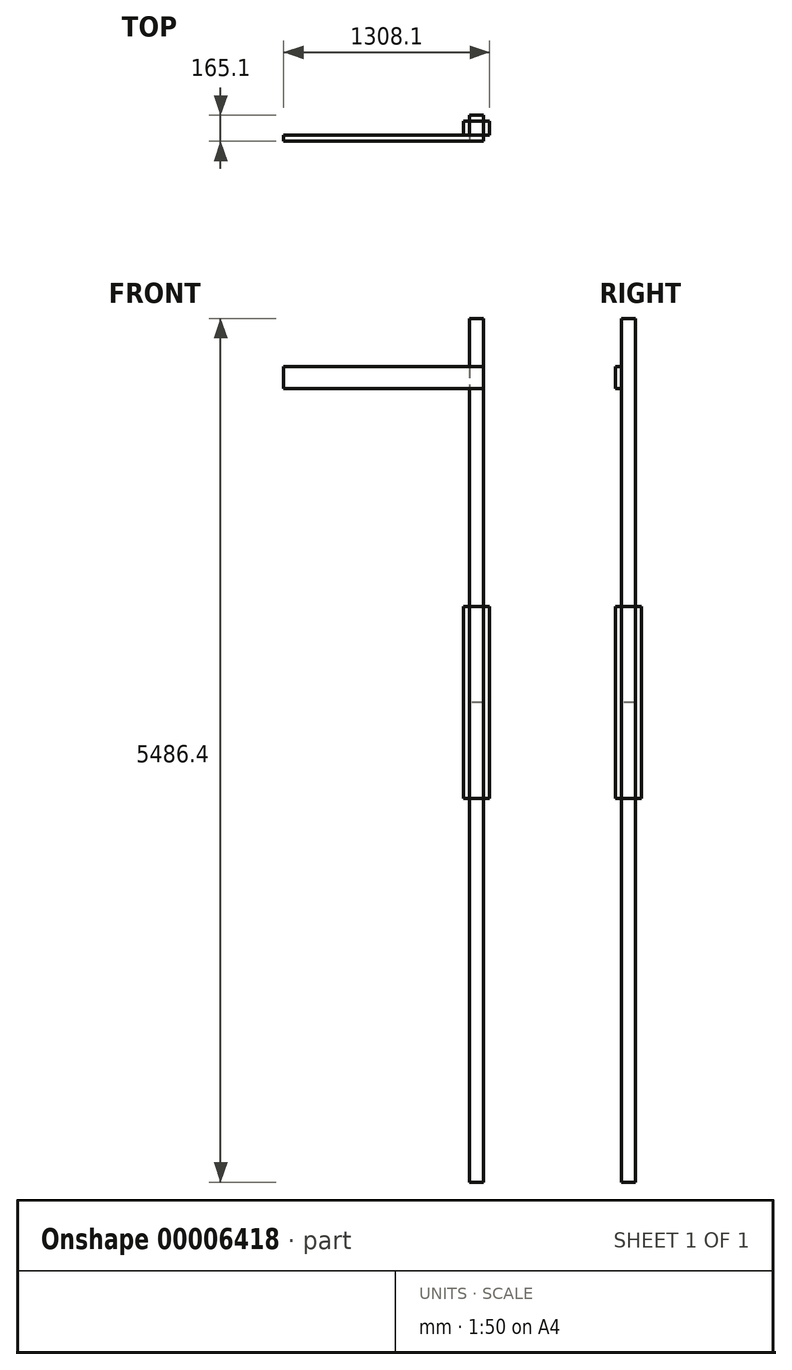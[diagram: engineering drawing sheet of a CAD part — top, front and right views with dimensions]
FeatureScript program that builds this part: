
annotation { "Feature Type Name" : "Feature", "Feature Type Description" : "" }
export const myFeature = defineFeature(function(context is Context, id is Id, definition is map)
    precondition{}
    {
        {
            var Q0;
            Q0=qCreatedBy(makeId("Top.planeOp"),FACE);
            var sketch = newSketch(context, id + "F0", { "sketchPlane" : qUnion([Q0])});
            skLineSegment(sketch, "E0.rect.bottom", {"start": v(44.45, 44.45) * mm, "end": v(-44.45, 44.45) * mm});
            skLineSegment(sketch, "E0.rect.top", {"start": v(44.45, -44.45) * mm, "end": v(-44.45, -44.45) * mm});
            skLineSegment(sketch, "E0.rect.left", {"start": v(44.45, 44.45) * mm, "end": v(44.45, -44.45) * mm});
            skLineSegment(sketch, "E0.rect.right", {"start": v(-44.45, 44.45) * mm, "end": v(-44.45, -44.45) * mm});
            skPoint(sketch, "E0.rect.middle", {"position": v(0, 0) * mm});
            skSolve(sketch);
        }
        {
            var Q0;
            Q0=makeQuery(id+"F0.imprint","IMPRINT",FACE,{"disambiguationData":[TD([[makeQuery(id+"F0.imprint","IMPRINT",EDGE,{"derivedFrom":sQuery(id+"F0.wireOp",EDGE,"E0.rect.bottom")}),1.0]])]});
            extrude(context, id + "F1", {"entities" : qUnion([Q0]), "depth" : 3048 * mm});
        }
        {
            var Q0;
            Q0=makeQuery(id+"F1.opExtrude","CAP_FACE",FACE,{"disambiguationData":[OSD([sQuery(id+"F0.wireOp",EDGE,"E0.rect.bottom"),sQuery(id+"F0.wireOp",EDGE,"E0.rect.top"),sQuery(id+"F0.wireOp",EDGE,"E0.rect.left"),sQuery(id+"F0.wireOp",EDGE,"E0.rect.right")])],"isStart":false});
            cPlane(context, id + "F2", {"entities" : qUnion([Q0]), "cplaneType" : CPlaneType.OFFSET, "offset" : 609.6 * mm, "oppositeDirection" : true, "width" : 152.4 * mm, "height" : 152.4 * mm});
        }
        {
            var Q0;
            Q0=qCreatedBy(id+"F2.planeOp",FACE);
            var sketch = newSketch(context, id + "F3", { "sketchPlane" : qUnion([Q0])});
            skLineSegment(sketch, "E1.0.0", {"start": v(44.45, 44.45) * mm, "end": v(44.45, -44.45) * mm});
            skLineSegment(sketch, "E2.bottom", {"start": v(44.45, -44.45) * mm, "end": v(82.55, -44.45) * mm});
            skLineSegment(sketch, "E2.top", {"start": v(44.45, 44.45) * mm, "end": v(82.55, 44.45) * mm});
            skLineSegment(sketch, "E2.left", {"start": v(44.45, -44.45) * mm, "end": v(44.45, 44.45) * mm});
            skLineSegment(sketch, "E2.right", {"start": v(82.55, -44.45) * mm, "end": v(82.55, 44.45) * mm});
            skSolve(sketch);
        }
        {
            var Q0;
            Q0=makeQuery(id+"F3.imprint","IMPRINT",FACE,{"disambiguationData":[TD([[makeQuery(id+"F3.imprint","IMPRINT",EDGE,{"derivedFrom":sQuery(id+"F3.wireOp",EDGE,"E2.bottom")}),1.0]])]});
            extrude(context, id + "F4", {"entities" : qUnion([Q0]), "depth" : 1219.2 * mm});
        }
        {
            var Q0;
            Q0=qCreatedBy(makeId("Front.planeOp"),FACE);
            var sketch = newSketch(context, id + "F5", { "sketchPlane" : qUnion([Q0])});
            skLineSegment(sketch, "E3", {"start": v(0, 0) * mm, "end": v(0, -138.6) * mm, "construction": true});
            skSolve(sketch);
        }
        {
            var Q0;
            Q0=makeQuery(id+"F1.opExtrude","CAP_FACE",FACE,{"disambiguationData":[OSD([sQuery(id+"F0.wireOp",EDGE,"E0.rect.bottom"),sQuery(id+"F0.wireOp",EDGE,"E0.rect.top"),sQuery(id+"F0.wireOp",EDGE,"E0.rect.left"),sQuery(id+"F0.wireOp",EDGE,"E0.rect.right")])],"isStart":false});
            var sketch = newSketch(context, id + "F6", { "sketchPlane" : qUnion([Q0])});
            skLineSegment(sketch, "E4.bottom", {"start": v(-44.45, -44.45) * mm, "end": v(44.45, -44.45) * mm});
            skLineSegment(sketch, "E4.top", {"start": v(-44.45, 44.45) * mm, "end": v(44.45, 44.45) * mm});
            skLineSegment(sketch, "E4.left", {"start": v(-44.45, -44.45) * mm, "end": v(-44.45, 44.45) * mm});
            skLineSegment(sketch, "E4.right", {"start": v(44.45, -44.45) * mm, "end": v(44.45, 44.45) * mm});
            skSolve(sketch);
        }
        {
            var Q0;
            Q0=makeQuery(id+"F6.imprint","IMPRINT",FACE,{"disambiguationData":[TD([[makeQuery(id+"F6.imprint","IMPRINT",EDGE,{"derivedFrom":sQuery(id+"F6.wireOp",EDGE,"E4.bottom")}),-1.0]])]});
            extrude(context, id + "F7", {"entities" : qUnion([Q0]), "depth" : 2438.4 * mm});
        }
        {
            var Q0;
            Q0=makeQuery(id+"F4.opExtrude","SWEPT_BODY",BODY,{"disambiguationData":[OSD([sQuery(id+"F3.wireOp",EDGE,"E2.bottom"),sQuery(id+"F3.wireOp",EDGE,"E2.top"),sQuery(id+"F3.wireOp",EDGE,"E2.left"),sQuery(id+"F3.wireOp",EDGE,"E2.right")])]});
            var Q1;
            Q1=makeQuery(id+"FR1GvV9cY72cUo5_3.opExtrude","SWEPT_BODY",BODY,{"disambiguationData":[OSD([sQuery(id+"Fx0JtN3gMRifMKx_3.wireOp",EDGE,"1e4fa40f-9285-4ff4-9127-986e21447ed7.bottom"),sQuery(id+"Fx0JtN3gMRifMKx_3.wireOp",EDGE,"1e4fa40f-9285-4ff4-9127-986e21447ed7.top"),sQuery(id+"Fx0JtN3gMRifMKx_3.wireOp",EDGE,"1e4fa40f-9285-4ff4-9127-986e21447ed7.left"),sQuery(id+"Fx0JtN3gMRifMKx_3.wireOp",EDGE,"1e4fa40f-9285-4ff4-9127-986e21447ed7.right")])]});
            var Q2;
            Q2=sQuery(id+"F5.wireOp",EDGE,"E3");
            circularPattern(context, id + "F8", {"entities" : qUnion([Q0, Q1]), "axis" : qUnion([Q2]), "angle" : 90 * degree, "instanceCount" : round(4)});
        }
        {
            var Q0;
            Q0=makeQuery(id+"F7.opExtrude","SWEPT_FACE",FACE,{"disambiguationData":[OSD([sQuery(id+"F6.wireOp",EDGE,"E4.bottom")])]});
            var sketch = newSketch(context, id + "F9", { "sketchPlane" : qUnion([Q0])});
            skLineSegment(sketch, "E5.bottom", {"start": v(44.45, 5181.6) * mm, "end": v(-1225.55, 5181.6) * mm});
            skLineSegment(sketch, "E5.top", {"start": v(44.45, 5041.9) * mm, "end": v(-1225.55, 5041.9) * mm});
            skLineSegment(sketch, "E5.left", {"start": v(44.45, 5181.6) * mm, "end": v(44.45, 5041.9) * mm});
            skLineSegment(sketch, "E5.right", {"start": v(-1225.55, 5181.6) * mm, "end": v(-1225.55, 5041.9) * mm});
            skSolve(sketch);
        }
        {
            var Q0;
            {var subQ6=sQuery(id+"F9.wireOp",EDGE,"E5.left");Q0=makeQuery(id+"F9.imprint","IMPRINT",FACE,{"disambiguationData":[TD([[makeQuery(id+"F9.imprint","IMPRINT",EDGE,{"derivedFrom":subQ6}),-1.0]])]});}
            var Q1;
            {var subQ5=sQuery(id+"F9.wireOp",EDGE,"E5.right");Q1=makeQuery(id+"F9.imprint","IMPRINT",FACE,{"disambiguationData":[TD([[makeQuery(id+"F9.imprint","IMPRINT",EDGE,{"derivedFrom":subQ5}),1.0]])]});}
            extrude(context, id + "F10", {"entities" : qUnion([Q0, Q1]), "depth" : 38.1 * mm});
        }
    });
